# Revit family: Bombito
name_source: partatom
category: Furniture
revit_build: Autodesk Revit 2014 (Build: 20130308_1515(x64)
units: mm (PartAtom-declared; Revit-internal decimal feet)

## types (2) — shared parameters
Chair Seat = 58
Keynote = XBF.2
Leg = Skandiform Chrome
Manufacturer = Skandiform AB
Type Comments = Created by Astacus AB
URL = http://www.biminfo.se

## per-type parameters (varying)
| type | Chair Legs | Description | Seat |
| KS-159 | Leg-arm | S-058 and KS-158 in birch, stained as option. S-059 and KS-159 are upholstered.
Underframe in chromium or silver lacquered metal.
Bar stool in black laminate K1015UN. Chassis in chromium. | Skandiform Fabric |
| S-059 | Leg | S-058 and KS-158 in birch, stained as option. S-059 and KS-159 are upholstered.
Underframe in chromium or silver lacquered metal. | Skandiform Chrome |

note: column(s) folded — value = type name in every type: Model

## geometry (parser evidence)
native form markers: Blend x15, Sweep x5
no freeform markers — native parametric forms only
